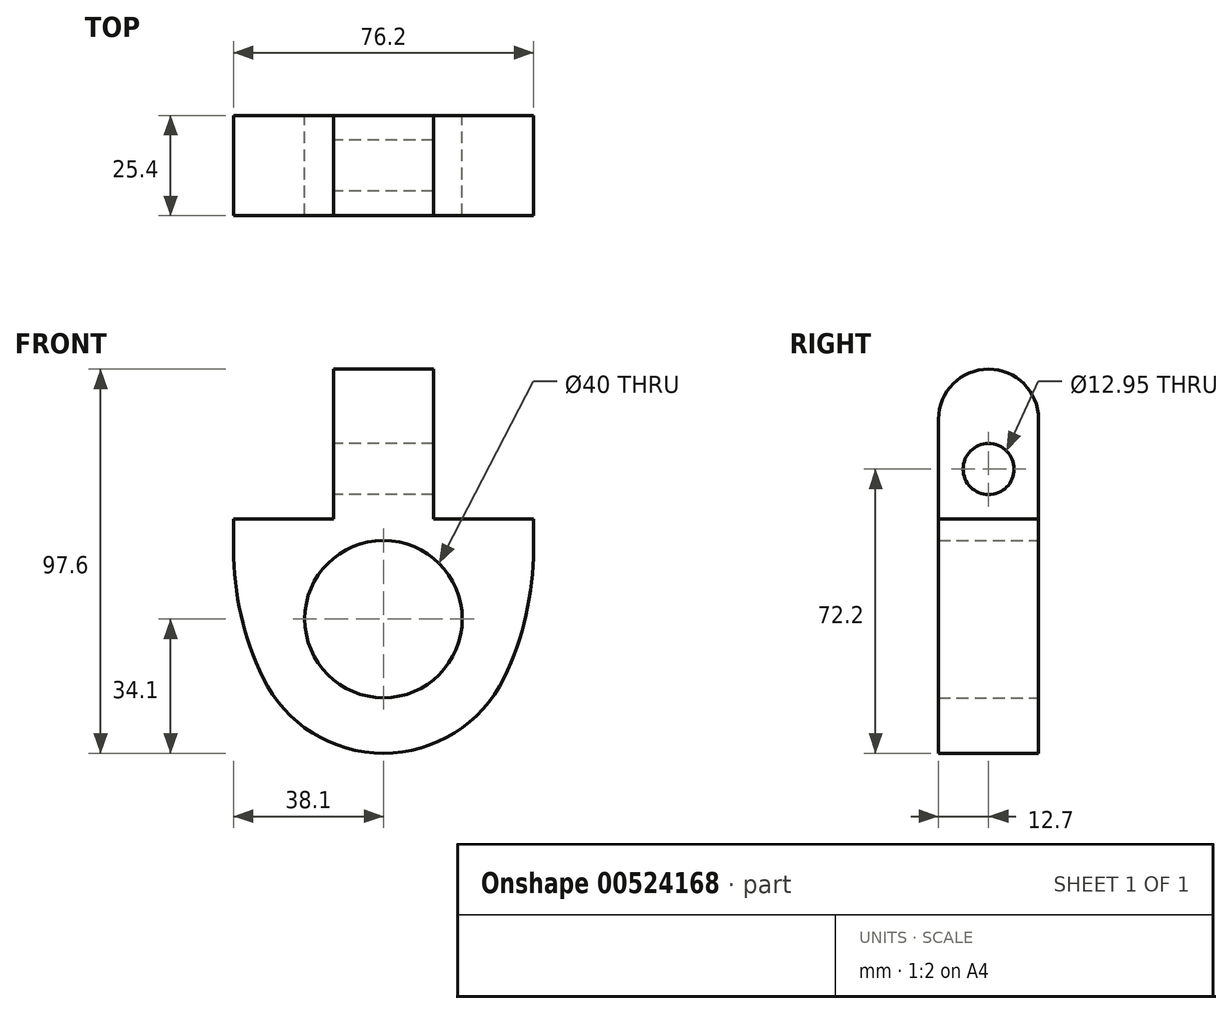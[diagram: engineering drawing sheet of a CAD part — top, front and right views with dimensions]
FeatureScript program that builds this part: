
annotation { "Feature Type Name" : "Feature", "Feature Type Description" : "" }
export const myFeature = defineFeature(function(context is Context, id is Id, definition is map)
    precondition{}
    {
        {
            var Q0;
            Q0=qCreatedBy(makeId("Front.planeOp"),FACE);
            var sketch = newSketch(context, id + "F0", { "sketchPlane" : qUnion([Q0])});
            skCircle(sketch, "E0", {"center": v(0, 0) * mm, "radius": 20 * mm});
            skArc(sketch, "E1", {"start": v(-30.64, -14.96) * mm, "mid": v(0, -34.1) * mm, "end": v(30.64, -14.96) * mm});
            skLineSegment(sketch, "E2", {"start": v(-38.1, 17.78) * mm, "end": v(-38.1, 25.4) * mm});
            skLineSegment(sketch, "E3", {"start": v(38.1, 17.78) * mm, "end": v(38.1, 25.4) * mm});
            skLineSegment(sketch, "E4", {"start": v(-38.1, 25.4) * mm, "end": v(-12.7, 25.4) * mm});
            skLineSegment(sketch, "E5.top", {"start": v(-12.7, 50.8) * mm, "end": v(12.7, 50.8) * mm});
            skLineSegment(sketch, "E5.left", {"start": v(-12.7, 25.4) * mm, "end": v(-12.7, 50.8) * mm});
            skLineSegment(sketch, "E5.right", {"start": v(12.7, 25.4) * mm, "end": v(12.7, 50.8) * mm});
            skLineSegment(sketch, "E6.trimOffspring", {"start": v(12.7, 25.4) * mm, "end": v(38.1, 25.4) * mm});
            skArc(sketch, "E7", {"start": v(-38.1, 17.78) * mm, "mid": v(-36.21, 0.99) * mm, "end": v(-30.64, -14.96) * mm});
            skArc(sketch, "E8", {"start": v(30.64, -14.96) * mm, "mid": v(36.21, 0.99) * mm, "end": v(38.1, 17.78) * mm});
            skSolve(sketch);
        }
        {
            var Q0;
            Q0=qSketchRegion(id+"F0",true);
            extrude(context, id + "F1", {"entities" : qUnion([Q0]), "endBound" : BoundingType.SYMMETRIC, "depth" : 25.4 * mm});
        }
        {
            var Q0;
            Q0=makeQuery(id+"F1.opExtrude","SWEPT_FACE",FACE,{"disambiguationData":[OSD([sQuery(id+"F0.wireOp",EDGE,"E5.left")])]});
            var sketch = newSketch(context, id + "F2", { "sketchPlane" : qUnion([Q0])});
            skCircle(sketch, "E9", {"center": v(0, 38.1) * mm, "radius": 6.48 * mm});
            skPoint(sketch, "E10.center.orphan", {"position": v(0, 50.8) * mm});
            skArc(sketch, "E11", {"start": v(12.7, 50.8) * mm, "mid": v(0, 63.5) * mm, "end": v(-12.7, 50.8) * mm});
            skLineSegment(sketch, "E12", {"start": v(-12.7, 50.8) * mm, "end": v(12.7, 50.8) * mm});
            skSolve(sketch);
        }
        {
            var Q0;
            Q0=makeQuery(id+"F2.imprint","IMPRINT",FACE,{"disambiguationData":[TD([[makeQuery(id+"F2.imprint","IMPRINT",EDGE,{"derivedFrom":sQuery(id+"F2.wireOp",EDGE,"E9")}),1.0]])]});
            extrude(context, id + "F3", {"entities" : qUnion([Q0]), "operationType" : NewBodyOperationType.REMOVE, "endBound" : BoundingType.THROUGH_ALL, "oppositeDirection" : true, "depth" : 25.4 * mm});
        }
        {
            var Q0;
            Q0=makeQuery(id+"F2.imprint","IMPRINT",FACE,{"disambiguationData":[TD([[makeQuery(id+"F2.imprint","IMPRINT",EDGE,{"derivedFrom":sQuery(id+"F2.wireOp",EDGE,"E11")}),1.0]])]});
            extrude(context, id + "F4", {"entities" : qUnion([Q0]), "operationType" : NewBodyOperationType.ADD, "oppositeDirection" : true, "depth" : 25.4 * mm});
        }
    });
